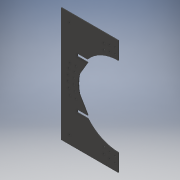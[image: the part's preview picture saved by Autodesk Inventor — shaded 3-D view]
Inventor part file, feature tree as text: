
AUTODESK INVENTOR PART (.ipt)
format: ipt  version: 2016 (Build 200138000, 138)  size: 377,344 bytes
history: native  units: in
note: dims shown in document units (in); Inventor stores cm internally (conversion verified against a paired STEP export)
features: sketch x6, extrude x5, reference x5, projected_geometry x4, hole x1
ambient origin geometry x8: Origin, YZ Plane, XZ Plane, XY Plane, X Axis, Y Axis, Z Axis, Center Point
bodies: Solid1 (feature_tree)
feature tree (21):
  extrude  "Extrusion1"  Depth=20.0in
  extrude  "Extrusion2"  Depth=0.5in
  hole  "Hole1"  [1 undecoded]
  extrude  "Extrusion3"  Depth=0.26in
  extrude  "Extrusion4"  Depth=1.5in
  extrude  "Extrusion5"  Depth=0.125in TaperAngle=0.0deg
  sketch  "Sketch1"  dims[d0=20.0in d3=0.26in]
  reference  "Reference1"
  reference  "Reference2"
  sketch  "Sketch2"  dims[d7=0.26in d8=0.5in]
  projected_geometry  "Projected Loop1"
  sketch  "Sketch3"  dims[d9=0.125in d10=0.0in d11=1.0in d12=0.0in]
  projected_geometry  "Projected Loop2"
  sketch  "Sketch4"  dims[d13=0.26in d14=0.75in d15=0.375in d16=0.25in d17=0.5635in d18=1.0in d19=0.8108in d20=0.26in]
  projected_geometry  "Projected Loop3"
  sketch  "Sketch5"  dims[d21=0.26in d22=1.5in]
  reference  "Reference3"
  sketch  "Sketch6"  dims[d23=1.5in d24=1.0in d25=0.0in d26=1.0in d27=0.0in d28=0.125in d29=0.0in]
  projected_geometry  "Projected Loop4"
  reference  "Reference4"
  reference  "Reference5"
note: 1 required parameter value undecoded (feature->parameter linkage not recoverable at this tier; creation-order binding heuristic only, values carry confidence <= 0.55)
